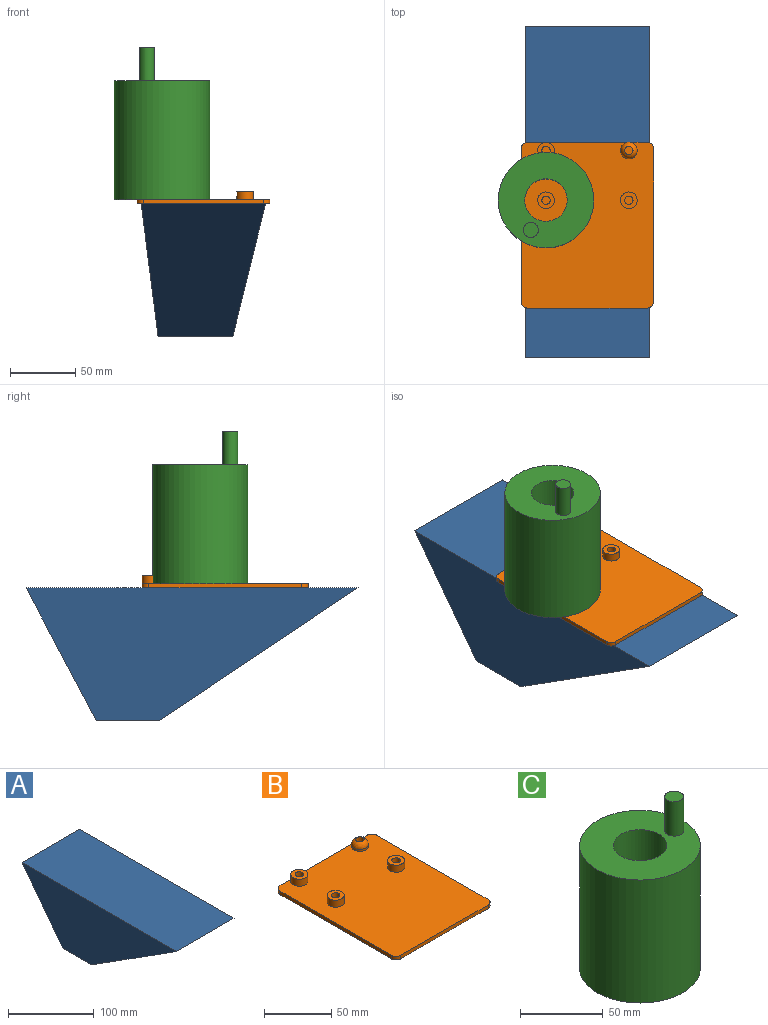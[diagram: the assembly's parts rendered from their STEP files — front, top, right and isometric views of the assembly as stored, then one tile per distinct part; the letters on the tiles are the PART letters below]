
ASSEMBLY  parts=3 mates=2
PART A: 6 faces, bbox 95.4x254.3x101.6 mm
  f0: plane 57.18x48.46mm, normal (0,0,-1), area 2771mm2, adj f2,f3,f4,f5
  f1: plane 254.31x95.39mm, normal (0,0,1), area 24258.3mm2, adj f2,f3,f4,f5
  f2: plane 101.6x95.39mm, normal (0,0.88,-0.47), area 8770.6mm2, adj f0,f1,f3,f5
  f3: plane 254.31x101.6mm, normal (-0.99,0,-0.13), area 15505.6mm2, adj f0,f1,f2,f4
  f4: plane 152.03x101.6mm, normal (0,-0.56,-0.83), area 13948.8mm2, adj f0,f1,f3,f5
  f5: plane 254.31x101.6mm, normal (0.97,0,-0.24), area 15847.8mm2, adj f0,f1,f2,f4
PART B: 26 faces, bbox 101.6x127x9.5 mm
  f0: plane 91.44x3.18mm, normal (0,1,0), area 290.3mm2, adj f4,f5,f22,f25
  f1: plane 116.84x3.18mm, normal (-1,0,0), area 371mm2, adj f4,f5,f22,f23
  f2: plane 91.44x3.18mm, normal (0,-1,0), area 290.3mm2, adj f4,f5,f23,f24
  f3: plane 116.84x3.18mm, normal (1,0,0), area 371mm2, adj f4,f5,f24,f25
  f4: plane 127x101.6mm, normal (0,0,1), area 12374.3mm2, adj f0,f1,f2,f3,f7,f11,f14,f18
  f5: plane 127x101.6mm, normal (0,0,-1), area 12881mm2, adj f0,f1,f2,f3,f22,f23,f24,f25
  f6: cylinder r=3.17mm len=6.35mm, axis (0,0,-1), area 126.7mm2, adj f8,f9
  f7: cylinder r=6.35mm len=12.7mm, axis (0,0,-1), area 253.4mm2, adj f4,f8
  f8: plane 12.7x12.7mm, normal (0,0,1), area 95mm2, adj f6,f7
  f9: plane 6.35x6.35mm, normal (0,0,1), area 31.7mm2, adj f6
  f10: cylinder r=3.17mm len=6.35mm, axis (0,0,-1), area 126.7mm2, adj f12,f21
  f11: cylinder r=6.35mm len=12.7mm, axis (0,0,-1), area 65.5mm2, adj f4,f21
  f12: plane 6.35x6.35mm, normal (0,0,1), area 31.7mm2, adj f10
  f13: cylinder r=3.17mm len=6.35mm, axis (0,0,-1), area 126.7mm2, adj f15,f16
  f14: cylinder r=6.35mm len=12.7mm, axis (0,0,-1), area 253.4mm2, adj f4,f15
  f15: plane 12.7x12.7mm, normal (0,0,1), area 95mm2, adj f13,f14
  f16: plane 6.35x6.35mm, normal (0,0,1), area 31.7mm2, adj f13
  f17: cylinder r=3.17mm len=6.35mm, axis (0,0,-1), area 126.7mm2, adj f19,f20
  f18: cylinder r=6.35mm len=12.7mm, axis (0,0,-1), area 253.4mm2, adj f4,f19
  f19: plane 12.7x12.7mm, normal (0,0,1), area 95mm2, adj f17,f18
  f20: plane 6.35x6.35mm, normal (0,0,1), area 31.7mm2, adj f17
  f21: torus R=1.27mm, axis (0,0,1), area 198.4mm2, adj f10,f11
  f22: cylinder r=5.08mm len=5.08mm, axis (0,0,1), area 25.3mm2, adj f0,f1,f4,f5
  f23: cylinder r=5.08mm len=5.08mm, axis (0,0,-1), area 25.3mm2, adj f1,f2,f4,f5
  f24: cylinder r=5.08mm len=5.08mm, axis (0,0,1), area 25.3mm2, adj f2,f3,f4,f5
  f25: cylinder r=5.08mm len=5.08mm, axis (0,0,-1), area 25.3mm2, adj f0,f3,f4,f5
PART C: 6 faces, bbox 73.1x73.1x116.6 mm
  f0: cylinder r=16.26mm len=91.19mm, axis (0,0,-1), area 9317mm2, adj f2,f3
  f1: cylinder r=36.57mm len=91.19mm, axis (0,0,-1), area 20953mm2, adj f2,f3
  f2: plane 73.14x73.14mm, normal (0,0,1), area 3268.2mm2, adj f0,f1,f4
  f3: plane 73.14x73.14mm, normal (0,0,-1), area 3370.9mm2, adj f0,f1
  f4: cylinder r=5.72mm len=25.4mm, axis (0,0,-1), area 912.8mm2, adj f2,f5
  f5: plane 11.44x11.44mm, normal (0,0,1), area 102.8mm2, adj f4
PLACE A t=(-42.68,68.34,-68.28)mm fixed
PLACE B t=(-36.08,-35.54,36.49)mm
PLACE C rot(axis=(0,0,-1),108.2deg) t=(40.61,89.24,-65.11)mm
MATE fastened B.f5 <-> A.f1  axis (0,0,-1) through (14.72,27.96,36.49)mm
MATE revolute B.f13 <-> C.f0  axis (0,0,1) through (-17.03,47.01,39.67)mm
